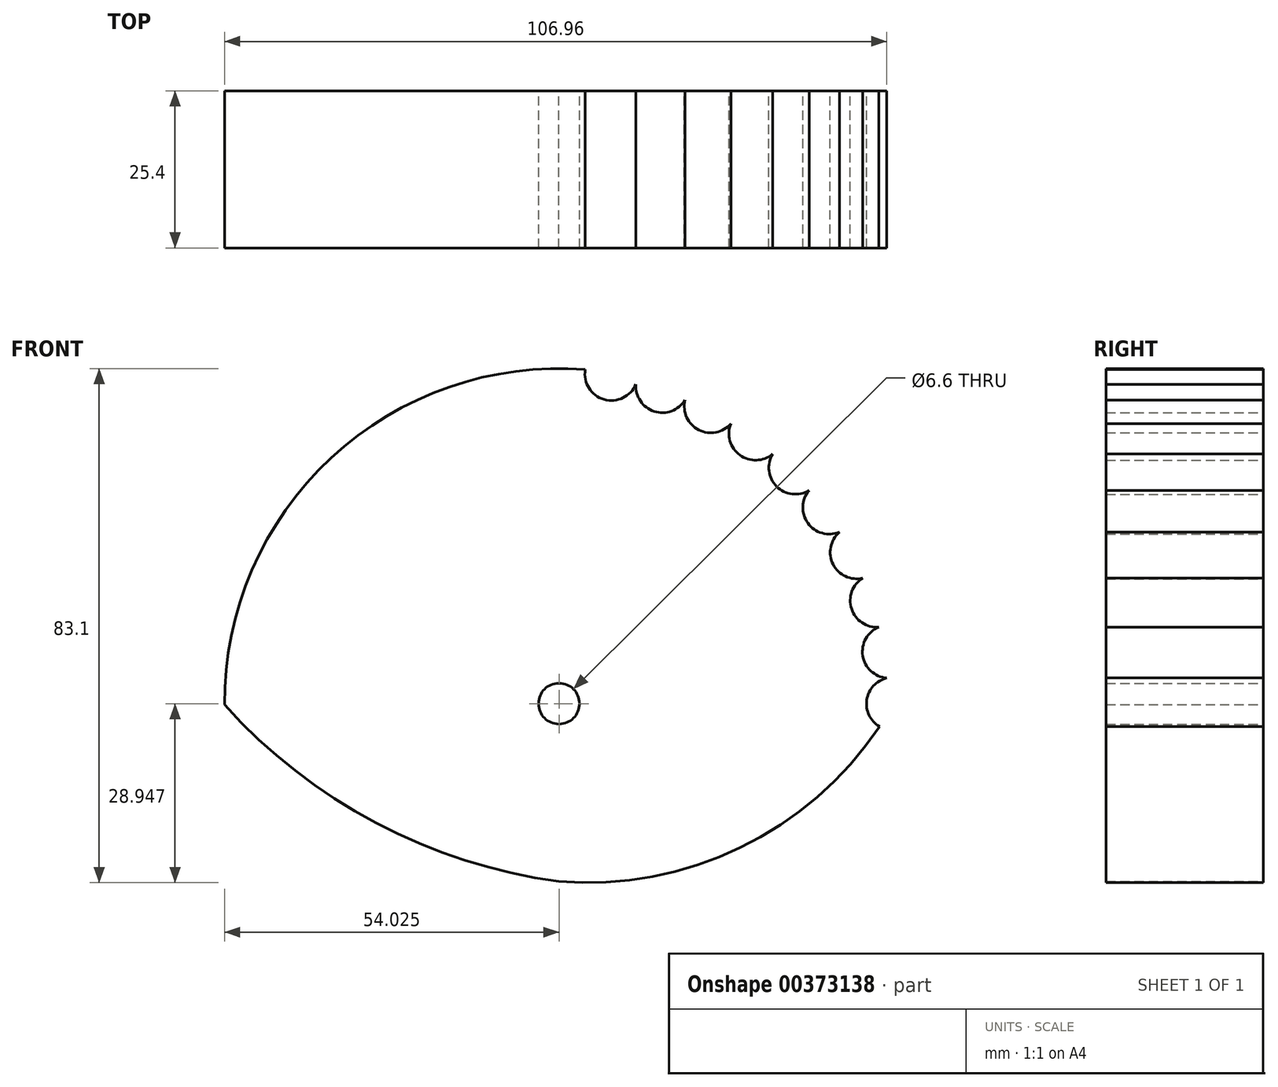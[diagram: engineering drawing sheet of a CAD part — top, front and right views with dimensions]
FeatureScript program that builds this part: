
annotation { "Feature Type Name" : "Feature", "Feature Type Description" : "" }
export const myFeature = defineFeature(function(context is Context, id is Id, definition is map)
    precondition{}
    {
        {
            var Q0;
            Q0=qCreatedBy(makeId("Front.planeOp"),FACE);
            var sketch = newSketch(context, id + "F0", { "sketchPlane" : qUnion([Q0])});
            skLineSegment(sketch, "E0", {"start": v(0, 0) * mm, "end": v(0, 53.97) * mm});
            skLineSegment(sketch, "E1", {"start": v(0, 0) * mm, "end": v(0, -28.58) * mm});
            skArc(sketch, "E2", {"start": v(0, -28.58) * mm, "mid": v(31.16, -22.18) * mm, "end": v(53.97, 0) * mm});
            skArc(sketch, "E3", {"start": v(-53.97, 0) * mm, "mid": v(-29.53, -19.08) * mm, "end": v(0, -28.58) * mm});
            skArc(sketch, "E4", {"start": v(53.97, 0) * mm, "mid": v(0, 54.34) * mm, "end": v(-53.97, 0) * mm});
            skCircle(sketch, "E5", {"center": v(53.34, 8.6) * mm, "radius": 4.3 * mm});
            skCircle(sketch, "E6.1.0", {"center": v(51.37, 16.83) * mm, "radius": 4.3 * mm});
            skCircle(sketch, "E6.2.0", {"center": v(48.14, 24.65) * mm, "radius": 4.3 * mm});
            skCircle(sketch, "E6.3.0", {"center": v(43.72, 31.88) * mm, "radius": 4.3 * mm});
            skCircle(sketch, "E6.4.0", {"center": v(38.22, 38.32) * mm, "radius": 4.3 * mm});
            skCircle(sketch, "E6.5.0", {"center": v(31.79, 43.82) * mm, "radius": 4.3 * mm});
            skCircle(sketch, "E6.6.0", {"center": v(24.57, 48.25) * mm, "radius": 4.3 * mm});
            skCircle(sketch, "E6.7.0", {"center": v(16.75, 51.5) * mm, "radius": 4.3 * mm});
            skCircle(sketch, "E6.8.0", {"center": v(8.52, 53.48) * mm, "radius": 4.3 * mm});
            skCircle(sketch, "E6.39.0", {"center": v(54, 0.15) * mm, "radius": 4.3 * mm});
            skPoint(sketch, "E6.center", {"position": v(0.04, 0.19) * mm});
            skCircle(sketch, "E7", {"center": v(0.04, 0.19) * mm, "radius": 3.3 * mm});
            skSolve(sketch);
        }
        {
            var Q0;
            {var subQ19=sQuery(id+"F0.wireOp",EDGE,"E3");Q0=makeQuery(id+"F0.imprint","IMPRINT",FACE,{"disambiguationData":[TD([[makeQuery(id+"F0.imprint","IMPRINT",EDGE,{"derivedFrom":subQ19}),1.0]])]});}
            extrude(context, id + "F1", {"entities" : qUnion([Q0]), "depth" : 25.4 * mm});
        }
    });
